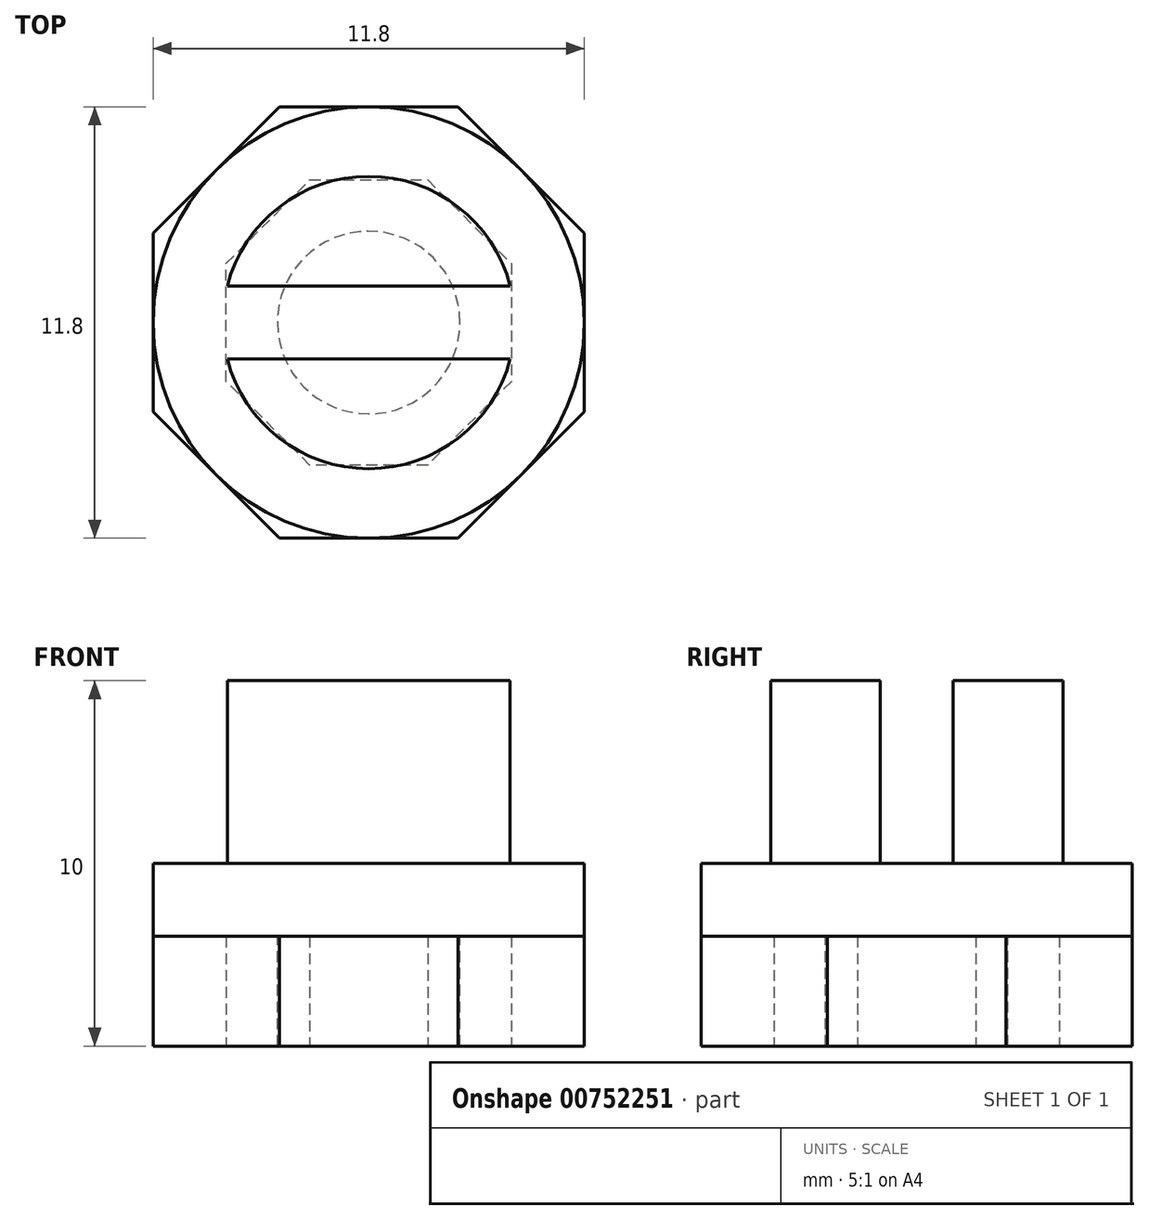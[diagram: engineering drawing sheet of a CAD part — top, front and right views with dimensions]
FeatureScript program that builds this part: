
annotation { "Feature Type Name" : "Feature", "Feature Type Description" : "" }
export const myFeature = defineFeature(function(context is Context, id is Id, definition is map)
    precondition{}
    {
        {
            var Q0;
            Q0=qCreatedBy(makeId("Top.planeOp"),FACE);
            var sketch = newSketch(context, id + "F0", { "sketchPlane" : qUnion([Q0])});
            skCircle(sketch, "E0.cCircle", {"center": v(0, 0) * mm, "radius": 3.9 * mm, "construction": true});
            skLineSegment(sketch, "E0.0", {"start": v(-3.9, -1.62) * mm, "end": v(-3.9, 1.62) * mm});
            skLineSegment(sketch, "E0.1", {"start": v(-3.9, 1.62) * mm, "end": v(-1.62, 3.9) * mm});
            skLineSegment(sketch, "E0.2", {"start": v(-1.62, 3.9) * mm, "end": v(1.62, 3.9) * mm});
            skLineSegment(sketch, "E0.3", {"start": v(1.62, 3.9) * mm, "end": v(3.9, 1.62) * mm});
            skLineSegment(sketch, "E0.4", {"start": v(3.9, 1.62) * mm, "end": v(3.9, -1.62) * mm});
            skLineSegment(sketch, "E0.5", {"start": v(3.9, -1.62) * mm, "end": v(1.62, -3.9) * mm});
            skLineSegment(sketch, "E0.6", {"start": v(1.62, -3.9) * mm, "end": v(-1.62, -3.9) * mm});
            skLineSegment(sketch, "E0.7", {"start": v(-1.62, -3.9) * mm, "end": v(-3.9, -1.62) * mm});
            skPoint(sketch, "E0.0.midPoint", {"position": v(-3.9, 0) * mm});
            skCircle(sketch, "E1.cCircle", {"center": v(0, 0) * mm, "radius": 5.9 * mm, "construction": true});
            skLineSegment(sketch, "E1.0", {"start": v(2.44, -5.9) * mm, "end": v(-2.44, -5.9) * mm});
            skLineSegment(sketch, "E1.1", {"start": v(-2.44, -5.9) * mm, "end": v(-5.9, -2.44) * mm});
            skLineSegment(sketch, "E1.2", {"start": v(-5.9, -2.44) * mm, "end": v(-5.9, 2.44) * mm});
            skLineSegment(sketch, "E1.3", {"start": v(-5.9, 2.44) * mm, "end": v(-2.44, 5.9) * mm});
            skLineSegment(sketch, "E1.4", {"start": v(-2.44, 5.9) * mm, "end": v(2.44, 5.9) * mm});
            skLineSegment(sketch, "E1.5", {"start": v(2.44, 5.9) * mm, "end": v(5.9, 2.44) * mm});
            skLineSegment(sketch, "E1.6", {"start": v(5.9, 2.44) * mm, "end": v(5.9, -2.44) * mm});
            skLineSegment(sketch, "E1.7", {"start": v(5.9, -2.44) * mm, "end": v(2.44, -5.9) * mm});
            skPoint(sketch, "E1.0.midPoint", {"position": v(0, -5.9) * mm});
            skCircle(sketch, "E2", {"center": v(0, 0) * mm, "radius": 2.6 * mm});
            skSolve(sketch);
        }
        {
            var Q0;
            Q0=qSketchRegion(id+"F0",true);
            extrude(context, id + "F1", {"entities" : qUnion([Q0]), "depth" : 3 * mm, "offsetDistance" : 25 * mm});
        }
        {
            var Q0;
            Q0=makeQuery(id+"F1.opExtrude","CAP_FACE",FACE,{"disambiguationData":[OSD([sQuery(id+"F0.wireOp",EDGE,"E0.0"),sQuery(id+"F0.wireOp",EDGE,"E0.1"),sQuery(id+"F0.wireOp",EDGE,"E0.2"),sQuery(id+"F0.wireOp",EDGE,"E0.3"),sQuery(id+"F0.wireOp",EDGE,"E0.4"),sQuery(id+"F0.wireOp",EDGE,"E0.5"),sQuery(id+"F0.wireOp",EDGE,"E0.6"),sQuery(id+"F0.wireOp",EDGE,"E0.7")])],"isStart":false});
            var sketch = newSketch(context, id + "F2", { "sketchPlane" : qUnion([Q0])});
            skCircle(sketch, "E3", {"center": v(0, 0) * mm, "radius": 5.9 * mm});
            skSolve(sketch);
        }
        {
            var Q0;
            Q0=qSketchRegion(id+"F2",true);
            extrude(context, id + "F3", {"entities" : qUnion([Q0]), "operationType" : NewBodyOperationType.ADD, "depth" : 2 * mm, "offsetDistance" : 25 * mm});
        }
        {
            var Q0;
            Q0=makeQuery(id+"F3.opExtrude","CAP_FACE",FACE,{"disambiguationData":[OSD([sQuery(id+"F2.wireOp",EDGE,"E3")])],"isStart":false});
            var sketch = newSketch(context, id + "F4", { "sketchPlane" : qUnion([Q0])});
            skLineSegment(sketch, "E4.bottom", {"start": v(3.87, -1) * mm, "end": v(-3.87, -1) * mm});
            skLineSegment(sketch, "E4.top", {"start": v(3.87, 1) * mm, "end": v(-3.87, 1) * mm});
            skPoint(sketch, "E4.middle", {"position": v(0, 0) * mm});
            skCircle(sketch, "E5", {"center": v(0, 0) * mm, "radius": 4 * mm});
            skSolve(sketch);
        }
        {
            var Q0;
            {var subQ0=sQuery(id+"F4.wireOp",EDGE,"E4.top");Q0=makeQuery(id+"F4.imprint","IMPRINT",FACE,{"disambiguationData":[TD([[makeQuery(id+"F4.imprint","IMPRINT",EDGE,{"derivedFrom":subQ0}),-1.0]])]});}
            var Q1;
            {var subQ0=sQuery(id+"F4.wireOp",EDGE,"E4.bottom");Q1=makeQuery(id+"F4.imprint","IMPRINT",FACE,{"disambiguationData":[TD([[makeQuery(id+"F4.imprint","IMPRINT",EDGE,{"derivedFrom":subQ0}),1.0]])]});}
            extrude(context, id + "F5", {"entities" : qUnion([Q0, Q1]), "operationType" : NewBodyOperationType.ADD, "depth" : 5 * mm, "offsetDistance" : 25 * mm});
        }
        {
            var Q0;
            Q0=makeQuery(id+"F3.opExtrude","CAP_FACE",FACE,{"disambiguationData":[OSD([sQuery(id+"F2.wireOp",EDGE,"E3")])],"isStart":true});
            var sketch = newSketch(context, id + "F6", { "sketchPlane" : qUnion([Q0])});
            skCircle(sketch, "E6", {"center": v(0, 0) * mm, "radius": 2.5 * mm});
            skSolve(sketch);
        }
        {
            var Q0;
            Q0=qSketchRegion(id+"F6",true);
            var Q1;
            Q1=makeQuery(id+"F1.opExtrude","CAP_FACE",FACE,{"disambiguationData":[OSD([sQuery(id+"F0.wireOp",EDGE,"E0.0"),sQuery(id+"F0.wireOp",EDGE,"E0.1"),sQuery(id+"F0.wireOp",EDGE,"E0.2"),sQuery(id+"F0.wireOp",EDGE,"E0.3"),sQuery(id+"F0.wireOp",EDGE,"E0.4"),sQuery(id+"F0.wireOp",EDGE,"E0.5"),sQuery(id+"F0.wireOp",EDGE,"E0.6"),sQuery(id+"F0.wireOp",EDGE,"E0.7"),sQuery(id+"F0.wireOp",EDGE,"E1.0"),sQuery(id+"F0.wireOp",EDGE,"E1.1"),sQuery(id+"F0.wireOp",EDGE,"E1.2"),sQuery(id+"F0.wireOp",EDGE,"E1.3"),sQuery(id+"F0.wireOp",EDGE,"E1.4"),sQuery(id+"F0.wireOp",EDGE,"E1.5"),sQuery(id+"F0.wireOp",EDGE,"E1.6"),sQuery(id+"F0.wireOp",EDGE,"E1.7")])],"isStart":true});
            extrude(context, id + "F7", {"entities" : qUnion([Q0]), "operationType" : NewBodyOperationType.ADD, "endBound" : BoundingType.UP_TO_SURFACE, "depth" : 2 * mm, "endBoundEntityFace" : qUnion([Q1]), "offsetDistance" : 25 * mm});
        }
    });
